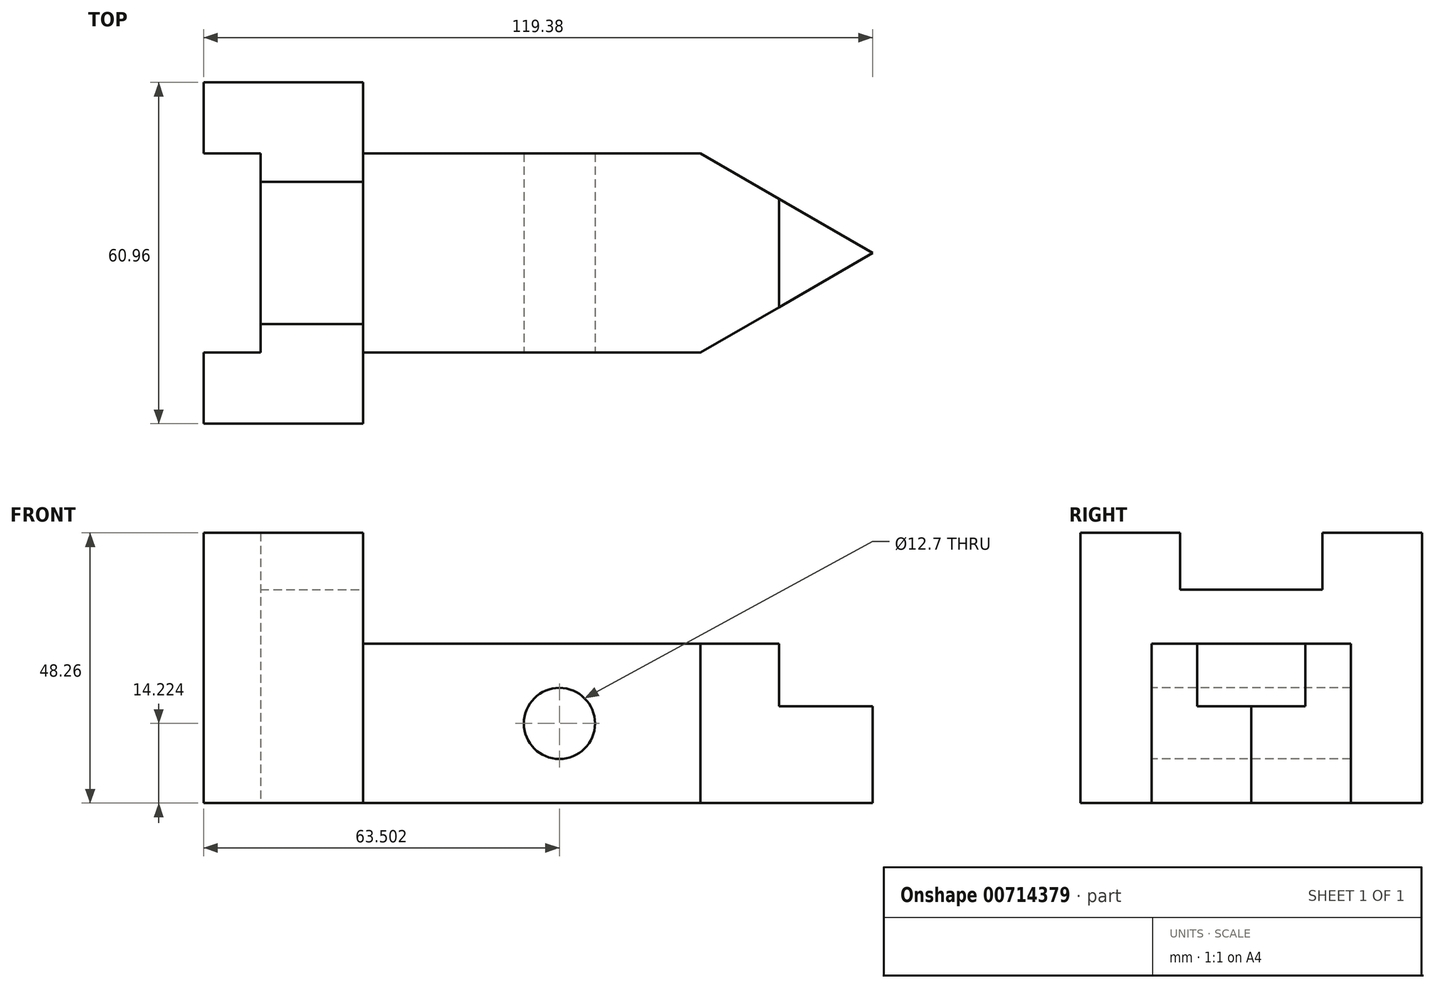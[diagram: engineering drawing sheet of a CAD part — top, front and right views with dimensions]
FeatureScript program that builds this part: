
annotation { "Feature Type Name" : "Feature", "Feature Type Description" : "" }
export const myFeature = defineFeature(function(context is Context, id is Id, definition is map)
    precondition{}
    {
        {
            var Q0;
            Q0=qCreatedBy(makeId("Top.planeOp"),FACE);
            var sketch = newSketch(context, id + "F0", { "sketchPlane" : qUnion([Q0])});
            skLineSegment(sketch, "E0", {"start": v(0, 0) * mm, "end": v(-28.45, 0) * mm});
            skLineSegment(sketch, "E1", {"start": v(-28.45, 0) * mm, "end": v(-28.45, 12.7) * mm});
            skLineSegment(sketch, "E2", {"start": v(-28.45, 12.7) * mm, "end": v(-18.29, 12.7) * mm});
            skLineSegment(sketch, "E3", {"start": v(-18.29, 12.7) * mm, "end": v(-18.29, 17.78) * mm});
            skLineSegment(sketch, "E4", {"start": v(0, 0) * mm, "end": v(0, 30.48) * mm});
            skLineSegment(sketch, "E5", {"start": v(-18.29, 30.48) * mm, "end": v(-18.29, 17.78) * mm});
            skLineSegment(sketch, "E6.MirrorCS", {"start": v(-18.29, 30.48) * mm, "end": v(-18.29, 43.18) * mm});
            skLineSegment(sketch, "E7.MirrorCS", {"start": v(-18.29, 48.26) * mm, "end": v(-18.29, 43.18) * mm});
            skLineSegment(sketch, "E8.MirrorCS", {"start": v(-28.45, 60.96) * mm, "end": v(-28.45, 48.26) * mm});
            skLineSegment(sketch, "E9.MirrorCS", {"start": v(0, 60.96) * mm, "end": v(-28.45, 60.96) * mm});
            skLineSegment(sketch, "E10.MirrorCS", {"start": v(0, 60.96) * mm, "end": v(0, 30.48) * mm});
            skLineSegment(sketch, "E11.MirrorCS", {"start": v(-28.45, 48.26) * mm, "end": v(-18.29, 48.26) * mm});
            skSolve(sketch);
        }
        {
            var Q0;
            Q0 = qSketchRegion(id + "F0", true);
            extrude(context, id + "F1", {"entities" : qUnion([Q0]), "depth" : 48.26 * mm, "offsetDistance" : 25.4 * mm});
        }
        {
            var Q0;
            Q0=makeQuery(id+"F1.opExtrude","SWEPT_FACE",FACE,{"disambiguationData":[OSD([sQuery(id+"F0.wireOp",EDGE,"E4"),sQuery(id+"F0.wireOp",EDGE,"E10.MirrorCS")])]});
            var sketch = newSketch(context, id + "F2", { "sketchPlane" : qUnion([Q0])});
            skLineSegment(sketch, "E12", {"start": v(30.48, 38.1) * mm, "end": v(17.78, 38.1) * mm});
            skLineSegment(sketch, "E13", {"start": v(30.48, 38.1) * mm, "end": v(43.18, 38.1) * mm});
            skLineSegment(sketch, "E14", {"start": v(43.18, 38.1) * mm, "end": v(43.18, 48.26) * mm});
            skLineSegment(sketch, "E15", {"start": v(17.78, 38.1) * mm, "end": v(17.78, 48.26) * mm});
            skLineSegment(sketch, "E16", {"start": v(17.78, 48.26) * mm, "end": v(43.18, 48.26) * mm});
            skSolve(sketch);
        }
        {
            var Q0;
            Q0 = qSketchRegion(id + "F2", true);
            extrude(context, id + "F3", {"entities" : qUnion([Q0]), "operationType" : NewBodyOperationType.REMOVE, "endBound" : BoundingType.UP_TO_NEXT, "oppositeDirection" : true, "depth" : 25.4 * mm, "offsetDistance" : 25.4 * mm});
        }
        {
            var Q0;
            Q0=qCreatedBy(makeId("Top.planeOp"),FACE);
            var sketch = newSketch(context, id + "F4", { "sketchPlane" : qUnion([Q0])});
            skLineSegment(sketch, "E17", {"start": v(0, 0) * mm, "end": v(0, 30.48) * mm});
            skLineSegment(sketch, "E18", {"start": v(0, 30.48) * mm, "end": v(0, 48.26) * mm});
            skLineSegment(sketch, "E19", {"start": v(0, 48.26) * mm, "end": v(60.2, 48.26) * mm});
            skLineSegment(sketch, "E20", {"start": v(60.2, 48.26) * mm, "end": v(90.93, 30.48) * mm});
            skLineSegment(sketch, "E21.MirrorCS", {"start": v(60.2, 12.7) * mm, "end": v(90.93, 30.48) * mm});
            skLineSegment(sketch, "E22.MirrorCS", {"start": v(0, 12.7) * mm, "end": v(60.2, 12.7) * mm});
            skLineSegment(sketch, "E23.MirrorCS", {"start": v(0, 30.48) * mm, "end": v(0, 12.7) * mm});
            skLineSegment(sketch, "E24", {"start": v(0, 12.7) * mm, "end": v(0, 48.26) * mm});
            skSolve(sketch);
        }
        {
            var Q0;
            Q0 = qSketchRegion(id + "F4", true);
            extrude(context, id + "F5", {"entities" : qUnion([Q0]), "operationType" : NewBodyOperationType.ADD, "depth" : 28.45 * mm, "offsetDistance" : 25.4 * mm});
        }
        {
            var Q0;
            Q0=makeQuery(id+"F5.opExtrude","CAP_FACE",FACE,{"disambiguationData":[OSD([sQuery(id+"F4.wireOp",EDGE,"E19"),sQuery(id+"F4.wireOp",EDGE,"E20"),sQuery(id+"F4.wireOp",EDGE,"E21.MirrorCS"),sQuery(id+"F4.wireOp",EDGE,"E22.MirrorCS"),sQuery(id+"F4.wireOp",EDGE,"E24")])],"isStart":false});
            var sketch = newSketch(context, id + "F6", { "sketchPlane" : qUnion([Q0])});
            skLineSegment(sketch, "E25", {"start": v(90.93, 30.48) * mm, "end": v(74.22, 40.15) * mm});
            skLineSegment(sketch, "E26", {"start": v(74.22, 40.15) * mm, "end": v(74.22, 20.81) * mm});
            skLineSegment(sketch, "E27", {"start": v(74.22, 20.81) * mm, "end": v(90.93, 30.48) * mm});
            skSolve(sketch);
        }
        {
            var Q0;
            Q0 = qSketchRegion(id + "F6", true);
            extrude(context, id + "F7", {"entities" : qUnion([Q0]), "operationType" : NewBodyOperationType.REMOVE, "oppositeDirection" : true, "depth" : 11.18 * mm, "offsetDistance" : 25.4 * mm});
        }
        {
            var Q0;
            Q0=makeQuery(id+"F5.opExtrude","SWEPT_FACE",FACE,{"disambiguationData":[OSD([sQuery(id+"F4.wireOp",EDGE,"E22.MirrorCS")])]});
            var sketch = newSketch(context, id + "F8", { "sketchPlane" : qUnion([Q0])});
            skCircle(sketch, "E28", {"center": v(35.05, 14.22) * mm, "radius": 6.35 * mm});
            skSolve(sketch);
        }
        {
            var Q0;
            Q0 = qSketchRegion(id + "F8", true);
            extrude(context, id + "F9", {"entities" : qUnion([Q0]), "operationType" : NewBodyOperationType.REMOVE, "endBound" : BoundingType.UP_TO_NEXT, "oppositeDirection" : true, "depth" : 25.4 * mm, "offsetDistance" : 25.4 * mm});
        }
    });
